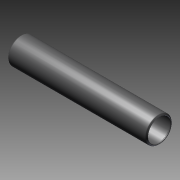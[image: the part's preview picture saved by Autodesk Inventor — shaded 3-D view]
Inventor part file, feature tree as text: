
AUTODESK INVENTOR PART (.ipt)
format: ipt  version: 2011 SP1 (Build 150282100, 282)  size: 126,464 bytes
history: native  units: in
note: dims shown in document units (in); Inventor stores cm internally (conversion verified against a paired STEP export)
features: other x42, revolve x1, sketch x1
ambient origin geometry x8: Origin, YZ Plane, XZ Plane, XY Plane, X Axis, Y Axis, Z Axis, Center Point
bodies: Solid1 (feature_tree)
feature tree (44):
  revolve  "Revolution1"  [1 undecoded]
  other  "cp1_XY"
  other  "cp1_YZ"
  other  "cp1_ZX"
  other  "cp1_X"
  other  "cp1_Y"
  other  "cp1_Z"
  other  "cp1_Center"
  other  "cp2_XY"
  other  "cp2_YZ"
  other  "cp2_ZX"
  other  "cp2_X"
  other  "cp2_Y"
  other  "cp2_Z"
  other  "cp2_Center"
  other  "cp3_XY"
  other  "cp3_YZ"
  other  "cp3_ZX"
  other  "cp3_X"
  other  "cp3_Y"
  other  "cp3_Z"
  other  "cp3_Center"
  other  "cp4_XY"
  other  "cp4_YZ"
  other  "cp4_ZX"
  other  "cp4_X"
  other  "cp4_Y"
  other  "cp4_Z"
  other  "cp4_Center"
  other  "tube_front_XY"
  other  "tube_front_YZ"
  other  "tube_front_ZX"
  other  "tube_front_X"
  other  "tube_front_Y"
  other  "tube_front_Z"
  other  "tube_front_Center"
  other  "tube_rear_XY"
  other  "tube_rear_YZ"
  other  "tube_rear_ZX"
  other  "tube_rear_X"
  other  "tube_rear_Y"
  other  "tube_rear_Z"
  other  "tube_rear_Center"
  sketch  "Sketch_1"  dims[d0=360.0deg]
note: 1 required parameter value undecoded (feature->parameter linkage not recoverable at this tier; creation-order binding heuristic only, values carry confidence <= 0.55)
